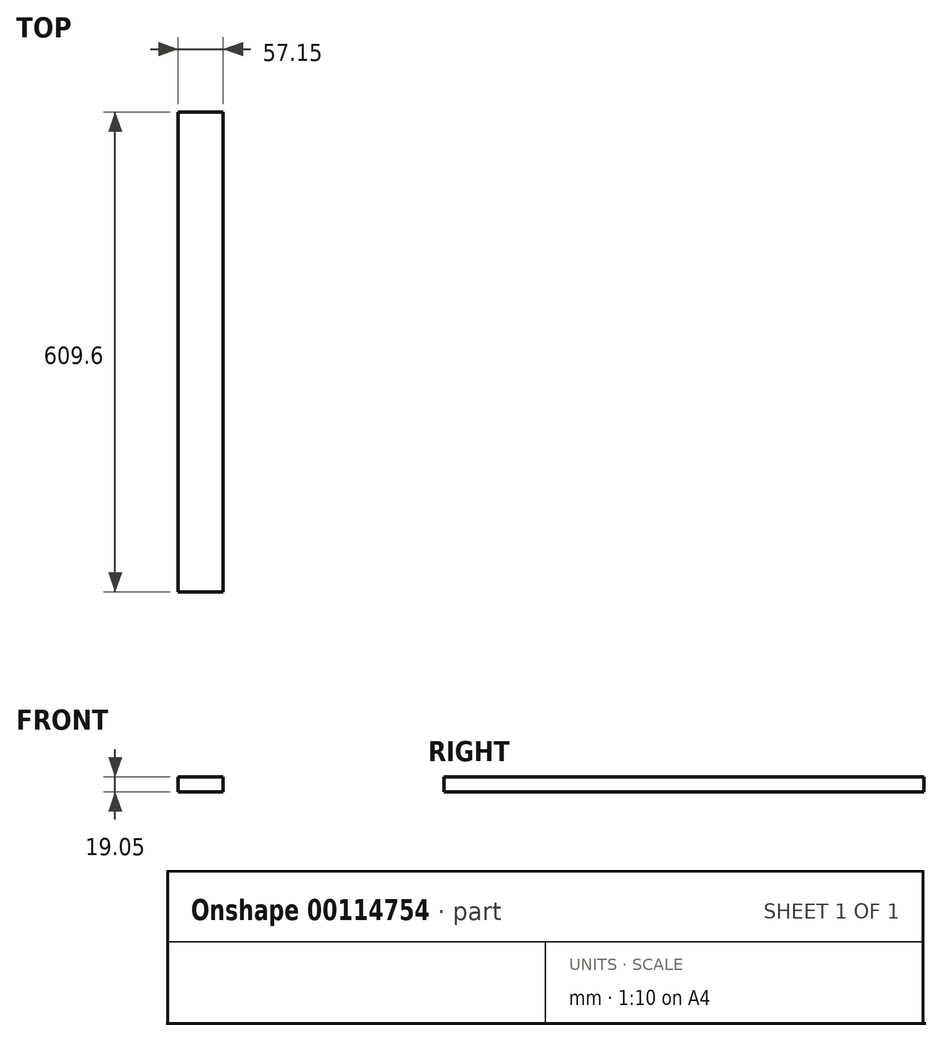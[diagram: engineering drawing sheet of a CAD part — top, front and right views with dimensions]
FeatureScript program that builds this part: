
annotation { "Feature Type Name" : "Feature", "Feature Type Description" : "" }
export const myFeature = defineFeature(function(context is Context, id is Id, definition is map)
    precondition{}
    {
        {
            var Q0;
            Q0=qCreatedBy(makeId("Top.planeOp"),FACE);
            var sketch = newSketch(context, id + "F0", { "sketchPlane" : qUnion([Q0])});
            skLineSegment(sketch, "E0.bottom", {"start": v(0, 0) * mm, "end": v(57.15, 0) * mm});
            skLineSegment(sketch, "E0.top", {"start": v(0, 609.6) * mm, "end": v(57.15, 609.6) * mm});
            skLineSegment(sketch, "E0.left", {"start": v(0, 0) * mm, "end": v(0, 609.6) * mm});
            skLineSegment(sketch, "E0.right", {"start": v(57.15, 0) * mm, "end": v(57.15, 609.6) * mm});
            skSolve(sketch);
        }
        {
            var Q0;
            Q0=qSketchRegion(id+"F0",true);
            extrude(context, id + "F1", {"entities" : qUnion([Q0]), "depth" : 19.05 * mm});
        }
    });
